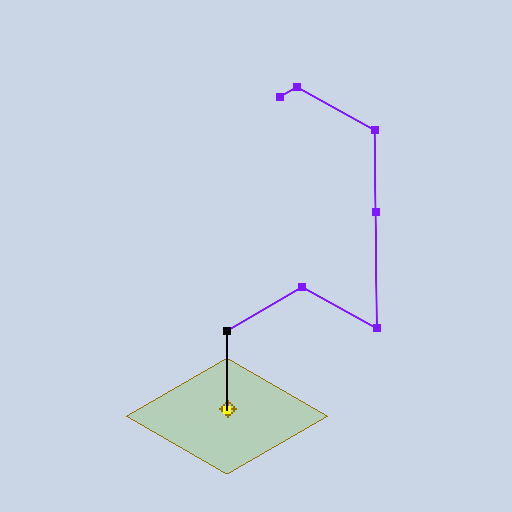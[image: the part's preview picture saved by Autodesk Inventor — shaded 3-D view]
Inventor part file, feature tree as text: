
AUTODESK INVENTOR PART (.ipt)
format: ipt  version: 2025 (Build 290162000, 162)  size: 106,496 bytes
history: native  units: in
note: dims shown in document units (in); Inventor stores cm internally (conversion verified against a paired STEP export)
features: other x1, plane x1, sketch x1
ambient origin geometry x8: Origin, YZ Plane, XZ Plane, XY Plane, X Axis, Y Axis, Z Axis, Center Point
feature tree (3):
  other  "Work Point1"
  plane  "Work Plane1"
  sketch  "3D Sketch1"
